# Revit family: Front_Load_Mailbox-Florence_Manufacturing-14High_Suite
name_source: partatom
category: Generic Models
revit_build: Autodesk Revit Architecture 2012 (Build: 20110916_2132(x64)
units: mm (PartAtom-declared; Revit-internal decimal feet)

## types (14) — shared parameters
Description = Front Load Mailbox
Door Material = Metal - Florence - Paint - Antique Bronze
Hardware = Metal - Florence - Steel
Height = 4' - 3 1/4"
Manufacturer = Florence Manufacturing
Minimum USPS Access Door = 1' - 3"
Mullion = 0' - 1 7/16"
Product Name = STD-4C
R Slot 7 = Empty
Unit Casing = Metal - Florence - Paint - Antique Bronze
Unit Casing Width = 4' - 2 5/16"
Width = 1' - 5"

## per-type parameters (varying)
- 4C14D-26: Center Mullion=Yes; Length=2' - 6 5/16"; R Slot 1-Top=Single Tenant Door; R Slot 10=Single Tenant Door; R Slot 11=Single Tenant Door; R Slot 12=Single Tenant Door; R Slot 13=Single Tenant Door; R Slot 14=Single Tenant Door; R Slot 2=Single Tenant Door; R Slot 3=Single Tenant Door; R Slot 4=Single Tenant Door; R Slot 5=Single Tenant Door; R Slot 6=Single Tenant Door; R Slot 8=Letter Drop; R Slot 9=Single Tenant Door; Side Frame Thickness=0' - 2 3/16"; Slot 1-Top=Single Tenant Door; Slot 10=Single Tenant Door; Slot 11=Single Tenant Door; Slot 12=Single Tenant Door; Slot 13=Single Tenant Door; Slot 14=Single Tenant Door; Slot 2=Single Tenant Door; Slot 3=Single Tenant Door; Slot 4=Single Tenant Door; Slot 5=Single Tenant Door; Slot 6=Single Tenant Door; Slot 7=Single Tenant Door; Slot 8=Single Tenant Door; Slot 9=Single Tenant Door
- 4C14BIN: Center Mullion=No; Length=1' - 4 1/4"; R Slot 1-Top=Empty; R Slot 10=Empty; R Slot 11=Empty; R Slot 12=Empty; R Slot 13=Empty; R Slot 14=Empty; R Slot 2=Empty; R Slot 3=Empty; R Slot 4=Empty; R Slot 5=Empty; R Slot 6=Empty; R Slot 8=Empty; R Slot 9=Empty; Side Frame Thickness=0' - 2 5/16"; Slot 1-Top=Empty; Slot 10=Empty; Slot 11=Empty; Slot 12=Empty; Slot 13=Empty; Slot 14=Fourteen High Trash Door; Slot 2=Empty; Slot 3=Empty; Slot 4=Empty; Slot 5=Empty; Slot 6=Empty; Slot 7=Empty; Slot 8=Empty; Slot 9=Empty
- 4C14HOP: Center Mullion=No; Length=1' - 4 1/4"; R Slot 1-Top=Empty; R Slot 10=Empty; R Slot 11=Empty; R Slot 12=Empty; R Slot 13=Empty; R Slot 14=Empty; R Slot 2=Empty; R Slot 3=Empty; R Slot 4=Empty; R Slot 5=Empty; R Slot 6=Empty; R Slot 8=Empty; R Slot 9=Empty; Side Frame Thickness=0' - 2 5/16"; Slot 1-Top=Empty; Slot 10=Empty; Slot 11=Empty; Slot 12=Empty; Slot 13=Empty; Slot 14=Fourteen HOP; Slot 2=Empty; Slot 3=Empty; Slot 4=Empty; Slot 5=Empty; Slot 6=Empty; Slot 7=Empty; Slot 8=Empty; Slot 9=Empty
- 4C14D-16: Center Mullion=Yes; Length=2' - 6 5/16"; R Slot 1-Top=Single Tenant Door; R Slot 10=Empty; R Slot 11=Empty; R Slot 12=Empty; R Slot 13=Empty; R Slot 14=Five High Single Parcel Locker; R Slot 2=Single Tenant Door; R Slot 3=Single Tenant Door; R Slot 4=Single Tenant Door; R Slot 5=Single Tenant Door; R Slot 6=Single Tenant Door; R Slot 8=Letter Drop; R Slot 9=Single Tenant Door; Side Frame Thickness=0' - 2 3/16"; Slot 1-Top=Single Tenant Door; Slot 10=Empty; Slot 11=Empty; Slot 12=Empty; Slot 13=Empty; Slot 14=Five High Single Parcel Locker; Slot 2=Single Tenant Door; Slot 3=Single Tenant Door; Slot 4=Single Tenant Door; Slot 5=Single Tenant Door; Slot 6=Single Tenant Door; Slot 7=Single Tenant Door; Slot 8=Single Tenant Door; Slot 9=Single Tenant Door
- 4C14S-03: Center Mullion=No; Length=1' - 4 1/4"; R Slot 1-Top=Empty; R Slot 10=Empty; R Slot 11=Empty; R Slot 12=Empty; R Slot 13=Empty; R Slot 14=Empty; R Slot 2=Empty; R Slot 3=Empty; R Slot 4=Empty; R Slot 5=Empty; R Slot 6=Empty; R Slot 8=Empty; R Slot 9=Empty; Side Frame Thickness=0' - 2 5/16"; Slot 1-Top=Empty; Slot 10=Empty; Slot 11=Empty; Slot 12=Empty; Slot 13=Empty; Slot 14=Six High Single Parcel Locker; Slot 2=Double Tenant Door; Slot 3=Empty; Slot 4=Double Tenant Door; Slot 5=Empty; Slot 6=Double Tenant Door; Slot 7=Empty; Slot 8=Letter Drop; Slot 9=Empty
- 4C14D-15: Center Mullion=Yes; Length=2' - 6 5/16"; R Slot 1-Top=Single Tenant Door; R Slot 10=Empty; R Slot 11=Empty; R Slot 12=Empty; R Slot 13=Empty; R Slot 14=Five High Single Parcel Locker; R Slot 2=Single Tenant Door; R Slot 3=Single Tenant Door; R Slot 4=Single Tenant Door; R Slot 5=Single Tenant Door; R Slot 6=Single Tenant Door; R Slot 8=Letter Drop; R Slot 9=Single Tenant Door; Side Frame Thickness=0' - 2 3/16"; Slot 1-Top=Single Tenant Door; Slot 10=Empty; Slot 11=Empty; Slot 12=Empty; Slot 13=Empty; Slot 14=Six High Single Parcel Locker; Slot 2=Single Tenant Door; Slot 3=Single Tenant Door; Slot 4=Single Tenant Door; Slot 5=Single Tenant Door; Slot 6=Single Tenant Door; Slot 7=Single Tenant Door; Slot 8=Single Tenant Door; Slot 9=Empty
- 4C14D-14: Center Mullion=Yes; Length=2' - 6 5/16"; R Slot 1-Top=Single Tenant Door; R Slot 10=Empty; R Slot 11=Empty; R Slot 12=Empty; R Slot 13=Empty; R Slot 14=Six High Single Parcel Locker; R Slot 2=Single Tenant Door; R Slot 3=Single Tenant Door; R Slot 4=Single Tenant Door; R Slot 5=Single Tenant Door; R Slot 6=Single Tenant Door; R Slot 8=Letter Drop; R Slot 9=Empty; Side Frame Thickness=0' - 2 3/16"; Slot 1-Top=Single Tenant Door; Slot 10=Empty; Slot 11=Empty; Slot 12=Empty; Slot 13=Empty; Slot 14=Six High Single Parcel Locker; Slot 2=Single Tenant Door; Slot 3=Single Tenant Door; Slot 4=Single Tenant Door; Slot 5=Single Tenant Door; Slot 6=Single Tenant Door; Slot 7=Single Tenant Door; Slot 8=Single Tenant Door; Slot 9=Empty
- 4C14D-13: Center Mullion=Yes; Length=2' - 6 5/16"; R Slot 1-Top=Empty; R Slot 10=Double Tenant Door; R Slot 11=Empty; R Slot 12=Double Tenant Door; R Slot 13=Empty; R Slot 14=Double Tenant Door; R Slot 2=Double Tenant Door; R Slot 3=Empty; R Slot 4=Double Tenant Door; R Slot 5=Empty; R Slot 6=Letter Drop; R Slot 8=Double Tenant Door; R Slot 9=Empty; Side Frame Thickness=0' - 2 3/16"; Slot 1-Top=Empty; Slot 10=Double Tenant Door; Slot 11=Empty; Slot 12=Double Tenant Door; Slot 13=Empty; Slot 14=Double Tenant Door; Slot 2=Double Tenant Door; Slot 3=Empty; Slot 4=Double Tenant Door; Slot 5=Empty; Slot 6=Double Tenant Door; Slot 7=Empty; Slot 8=Double Tenant Door; Slot 9=Empty
- 4C14S-12: Center Mullion=No; Length=1' - 4 1/4"; R Slot 1-Top=Empty; R Slot 10=Empty; R Slot 11=Empty; R Slot 12=Empty; R Slot 13=Empty; R Slot 14=Empty; R Slot 2=Empty; R Slot 3=Empty; R Slot 4=Empty; R Slot 5=Empty; R Slot 6=Empty; R Slot 8=Empty; R Slot 9=Empty; Side Frame Thickness=0' - 2 5/16"; Slot 1-Top=Single Tenant Door; Slot 10=Single Tenant Door; Slot 11=Single Tenant Door; Slot 12=Single Tenant Door; Slot 13=Single Tenant Door; Slot 14=Single Tenant Door; Slot 2=Single Tenant Door; Slot 3=Single Tenant Door; Slot 4=Single Tenant Door; Slot 5=Single Tenant Door; Slot 6=Single Tenant Door; Slot 7=Empty; Slot 8=Letter Drop; Slot 9=Single Tenant Door
- 4C14D-07: Center Mullion=Yes; Length=2' - 6 5/16"; R Slot 1-Top=Empty; R Slot 10=Empty; R Slot 11=Empty; R Slot 12=Empty; R Slot 13=Empty; R Slot 14=Six High Single Parcel Locker; R Slot 2=Double Tenant Door; R Slot 3=Empty; R Slot 4=Double Tenant Door; R Slot 5=Empty; R Slot 6=Double Tenant Door; R Slot 8=Letter Drop; R Slot 9=Empty; Side Frame Thickness=0' - 2 3/16"; Slot 1-Top=Empty; Slot 10=Empty; Slot 11=Empty; Slot 12=Empty; Slot 13=Empty; Slot 14=Six High Single Parcel Locker; Slot 2=Double Tenant Door; Slot 3=Empty; Slot 4=Double Tenant Door; Slot 5=Empty; Slot 6=Double Tenant Door; Slot 7=Empty; Slot 8=Double Tenant Door; Slot 9=Empty
- 4C14S-3P: Center Mullion=No; Length=1' - 4 1/4"; R Slot 1-Top=Empty; R Slot 10=Empty; R Slot 11=Empty; R Slot 12=Empty; R Slot 13=Empty; R Slot 14=Empty; R Slot 2=Empty; R Slot 3=Empty; R Slot 4=Empty; R Slot 5=Empty; R Slot 6=Empty; R Slot 8=Empty; R Slot 9=Empty; Side Frame Thickness=0' - 2 5/16"; Slot 1-Top=Empty; Slot 10=Empty; Slot 11=Empty; Slot 12=Empty; Slot 13=Empty; Slot 14=Five High Single Parcel Locker; Slot 2=Empty; Slot 3=Empty; Slot 4=Four High Single Parcel Locker; Slot 5=Empty; Slot 6=Empty; Slot 7=Empty; Slot 8=Empty; Slot 9=Five High Single Parcel Locker
- 4C14S-06: Center Mullion=No; Length=1' - 4 1/4"; R Slot 1-Top=Empty; R Slot 10=Empty; R Slot 11=Empty; R Slot 12=Empty; R Slot 13=Empty; R Slot 14=Empty; R Slot 2=Empty; R Slot 3=Empty; R Slot 4=Empty; R Slot 5=Empty; R Slot 6=Empty; R Slot 8=Empty; R Slot 9=Empty; Side Frame Thickness=0' - 2 5/16"; Slot 1-Top=Empty; Slot 10=Double Tenant Door; Slot 11=Empty; Slot 12=Double Tenant Door; Slot 13=Empty; Slot 14=Double Tenant Door; Slot 2=Double Tenant Door; Slot 3=Empty; Slot 4=Double Tenant Door; Slot 5=Empty; Slot 6=Double Tenant Door; Slot 7=Empty; Slot 8=Letter Drop; Slot 9=Empty
- 4C14S-07: Center Mullion=No; Length=1' - 4 1/4"; R Slot 1-Top=Empty; R Slot 10=Empty; R Slot 11=Empty; R Slot 12=Empty; R Slot 13=Empty; R Slot 14=Empty; R Slot 2=Empty; R Slot 3=Empty; R Slot 4=Empty; R Slot 5=Empty; R Slot 6=Empty; R Slot 8=Empty; R Slot 9=Empty; Side Frame Thickness=0' - 2 5/16"; Slot 1-Top=Single Tenant Door; Slot 10=Empty; Slot 11=Empty; Slot 12=Empty; Slot 13=Empty; Slot 14=Five High Single Parcel Locker; Slot 2=Single Tenant Door; Slot 3=Single Tenant Door; Slot 4=Single Tenant Door; Slot 5=Single Tenant Door; Slot 6=Single Tenant Door; Slot 7=Empty; Slot 8=Letter Drop; Slot 9=Single Tenant Door
- 4C14S-2P: Center Mullion=No; Length=1' - 4 1/4"; R Slot 1-Top=Empty; R Slot 10=Empty; R Slot 11=Empty; R Slot 12=Empty; R Slot 13=Empty; R Slot 14=Empty; R Slot 2=Empty; R Slot 3=Empty; R Slot 4=Empty; R Slot 5=Empty; R Slot 6=Empty; R Slot 8=Empty; R Slot 9=Empty; Side Frame Thickness=0' - 2 5/16"; Slot 1-Top=Empty; Slot 10=Empty; Slot 11=Empty; Slot 12=Empty; Slot 13=Empty; Slot 14=Six High Single Parcel Locker; Slot 2=Empty; Slot 3=Empty; Slot 4=Empty; Slot 5=Empty; Slot 6=Six High Single Parcel Locker; Slot 7=Empty; Slot 8=Letter Drop; Slot 9=Empty

note: column(s) folded — value = type name in every type: Model

## geometry (parser evidence)
native form markers: Blend x9, Sweep x32
no freeform markers — native parametric forms only
